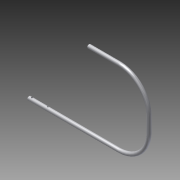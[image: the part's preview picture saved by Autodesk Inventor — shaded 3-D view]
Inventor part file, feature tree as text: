
AUTODESK INVENTOR PART (.ipt)
format: ipt  version: 2014 SP1 (Build 180222100, 222)  size: 147,968 bytes
history: native  units: in
note: dims shown in document units (in); Inventor stores cm internally (conversion verified against a paired STEP export)
features: sketch x3, sweep x1, plane x1, extrude x1
ambient origin geometry x8: Origin, YZ Plane, XZ Plane, XY Plane, X Axis, Y Axis, Z Axis, Center Point
bodies: Solid1 (feature_tree)
feature tree (6):
  sweep  "Sweep1"
  plane  "Work Plane1"
  extrude  "Extrusion1"  Depth=4.0in
  sketch  "Sketch1"  dims[d0=12.0in d1=4.0in]
  sketch  "Sketch2"  dims[d2=2.0in d3=4.0in]
  sketch  "Sketch3"  dims[d4=4.0in d5=0.5in d6=0.0in d7=25.0in d8=0.375in d9=0.164in d10=2.5in d11=0.25in d12=1.0in d13=0.0in d14=0.194in d15=0.375in d16=0.25in]
